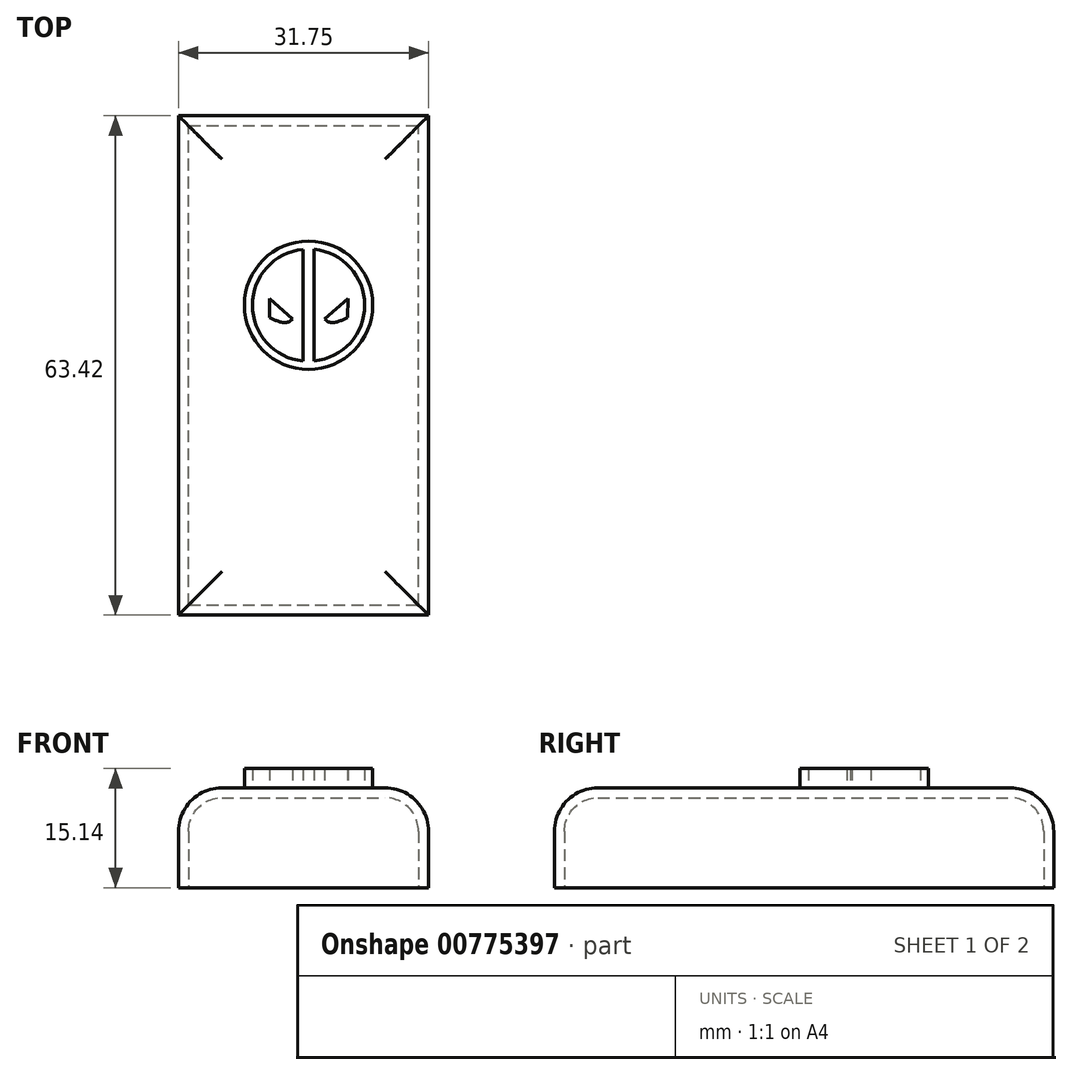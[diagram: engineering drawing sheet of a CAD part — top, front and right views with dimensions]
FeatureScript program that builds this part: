
annotation { "Feature Type Name" : "Feature", "Feature Type Description" : "" }
export const myFeature = defineFeature(function(context is Context, id is Id, definition is map)
    precondition{}
    {
        {
            var Q0;
            Q0=qCreatedBy(makeId("Top.planeOp"),FACE);
            var sketch = newSketch(context, id + "F0", { "sketchPlane" : qUnion([Q0])});
            skLineSegment(sketch, "E0", {"start": v(-16.52, -39.36) * mm, "end": v(15.23, -39.36) * mm});
            skLineSegment(sketch, "E1", {"start": v(-16.52, -39.36) * mm, "end": v(-16.52, 24.06) * mm});
            skLineSegment(sketch, "E2", {"start": v(15.23, -39.36) * mm, "end": v(15.23, 24.06) * mm});
            skLineSegment(sketch, "E3", {"start": v(-16.52, 24.06) * mm, "end": v(15.23, 24.06) * mm});
            skSolve(sketch);
        }
        {
            var Q0;
            Q0=makeQuery(id+"F0.imprint","IMPRINT",FACE,{"disambiguationData":[TD([[makeQuery(id+"F0.imprint","IMPRINT",EDGE,{"derivedFrom":sQuery(id+"F0.wireOp",EDGE,"E0")}),1.0]])]});
            extrude(context, id + "F1", {"entities" : qUnion([Q0]), "depth" : 12.7 * mm, "offsetDistance" : 25.4 * mm});
        }
        {
            var Q0;
            Q0=makeQuery(id+"F1.opExtrude","CAP_EDGE",EDGE,{"disambiguationData":[OSD([sQuery(id+"F0.wireOp",EDGE,"E1")])],"isStart":false});
            var Q1;
            Q1=makeQuery(id+"F1.opExtrude","CAP_EDGE",EDGE,{"disambiguationData":[OSD([sQuery(id+"F0.wireOp",EDGE,"E0")])],"isStart":false});
            var Q2;
            Q2=makeQuery(id+"F1.opExtrude","CAP_EDGE",EDGE,{"disambiguationData":[OSD([sQuery(id+"F0.wireOp",EDGE,"E2")])],"isStart":false});
            var Q3;
            Q3=makeQuery(id+"F1.opExtrude","CAP_EDGE",EDGE,{"disambiguationData":[OSD([sQuery(id+"F0.wireOp",EDGE,"E3")])],"isStart":false});
            fillet(context, id + "F2", {"entities" : qUnion([Q0, Q1, Q2, Q3]), "radius" : 5.52 * mm, "tangentPropagation" : true, "allowEdgeOverflow" : false});
        }
        {
            var Q0;
            Q0=makeQuery(id+"F1.opExtrude","CAP_FACE",FACE,{"disambiguationData":[OSD([sQuery(id+"F0.wireOp",EDGE,"E0"),sQuery(id+"F0.wireOp",EDGE,"E1"),sQuery(id+"F0.wireOp",EDGE,"E2"),sQuery(id+"F0.wireOp",EDGE,"E3")])],"isStart":true});
            shell(context, id + "F3", {"entities" : qUnion([Q0]), "thickness" : 1.27 * mm});
        }
        {
            var Q0;
            Q0=makeQuery(id+"F1.opExtrude","CAP_FACE",FACE,{"disambiguationData":[OSD([sQuery(id+"F0.wireOp",EDGE,"E0"),sQuery(id+"F0.wireOp",EDGE,"E1"),sQuery(id+"F0.wireOp",EDGE,"E2"),sQuery(id+"F0.wireOp",EDGE,"E3")])],"isStart":false});
            var sketch = newSketch(context, id + "F4", { "sketchPlane" : qUnion([Q0])});
            skCircle(sketch, "E4", {"center": v(0, 0) * mm, "radius": 8.15 * mm});
            skArc(sketch, "E5", {"start": v(-0.73, 7.1) * mm, "mid": v(-7.14, 0) * mm, "end": v(-0.73, -7.1) * mm});
            skLineSegment(sketch, "E6", {"start": v(-0.73, 7.1) * mm, "end": v(-0.73, -7.1) * mm});
            skLineSegment(sketch, "E7", {"start": v(0.71, 7.1) * mm, "end": v(0.73, -7.1) * mm});
            skLineSegment(sketch, "E8", {"start": v(-2.03, -1.75) * mm, "end": v(-4.99, 0.82) * mm});
            skArc(sketch, "E9.trimOffspring", {"start": v(0.73, -7.1) * mm, "mid": v(7.14, 0) * mm, "end": v(0.71, 7.1) * mm});
            skLineSegment(sketch, "E10", {"start": v(-4.99, 0.82) * mm, "end": v(-4.98, -1.59) * mm});
            skFitSpline(sketch, "E11", {"points": [v(-4.98, -1.59) * mm, v(-3.89, -2.03) * mm, v(-2.8, -2.19) * mm, v(-2.03, -1.75) * mm], "startDerivative": vector(3.02, -1.31) * mm, "endDerivative": vector(2.33, 1.87) * mm});
            skLineSegment(sketch, "E12.MirrorCS", {"start": v(2.03, -1.75) * mm, "end": v(4.99, 0.82) * mm});
            skFitSpline(sketch, "E13.MirrorCS", {"points": [v(4.98, -1.59) * mm, v(3.89, -2.03) * mm, v(2.8, -2.19) * mm, v(2.03, -1.75) * mm], "startDerivative": vector(-3.02, -1.31) * mm, "endDerivative": vector(-2.33, 1.87) * mm});
            skLineSegment(sketch, "E14.MirrorCS", {"start": v(4.99, 0.82) * mm, "end": v(4.98, -1.59) * mm});
            skSolve(sketch);
        }
        {
            var Q0;
            Q0=makeQuery(id+"F4.imprint","IMPRINT",FACE,{"disambiguationData":[TD([[makeQuery(id+"F4.imprint","IMPRINT",EDGE,{"derivedFrom":sQuery(id+"F4.wireOp",EDGE,"E4")}),1.0]])]});
            var Q1;
            Q1=makeQuery(id+"F4.imprint","IMPRINT",FACE,{"disambiguationData":[TD([[makeQuery(id+"F4.imprint","IMPRINT",EDGE,{"derivedFrom":sQuery(id+"F4.wireOp",EDGE,"E8")}),1.0]])]});
            var Q2;
            Q2=makeQuery(id+"F4.imprint","IMPRINT",FACE,{"disambiguationData":[TD([[makeQuery(id+"F4.imprint","IMPRINT",EDGE,{"derivedFrom":sQuery(id+"F4.wireOp",EDGE,"E12.MirrorCS")}),-1.0]])]});
            extrude(context, id + "F5", {"entities" : qUnion([Q0, Q1, Q2]), "operationType" : NewBodyOperationType.ADD, "depth" : 2.44 * mm, "offsetDistance" : 25.4 * mm});
        }
    });
